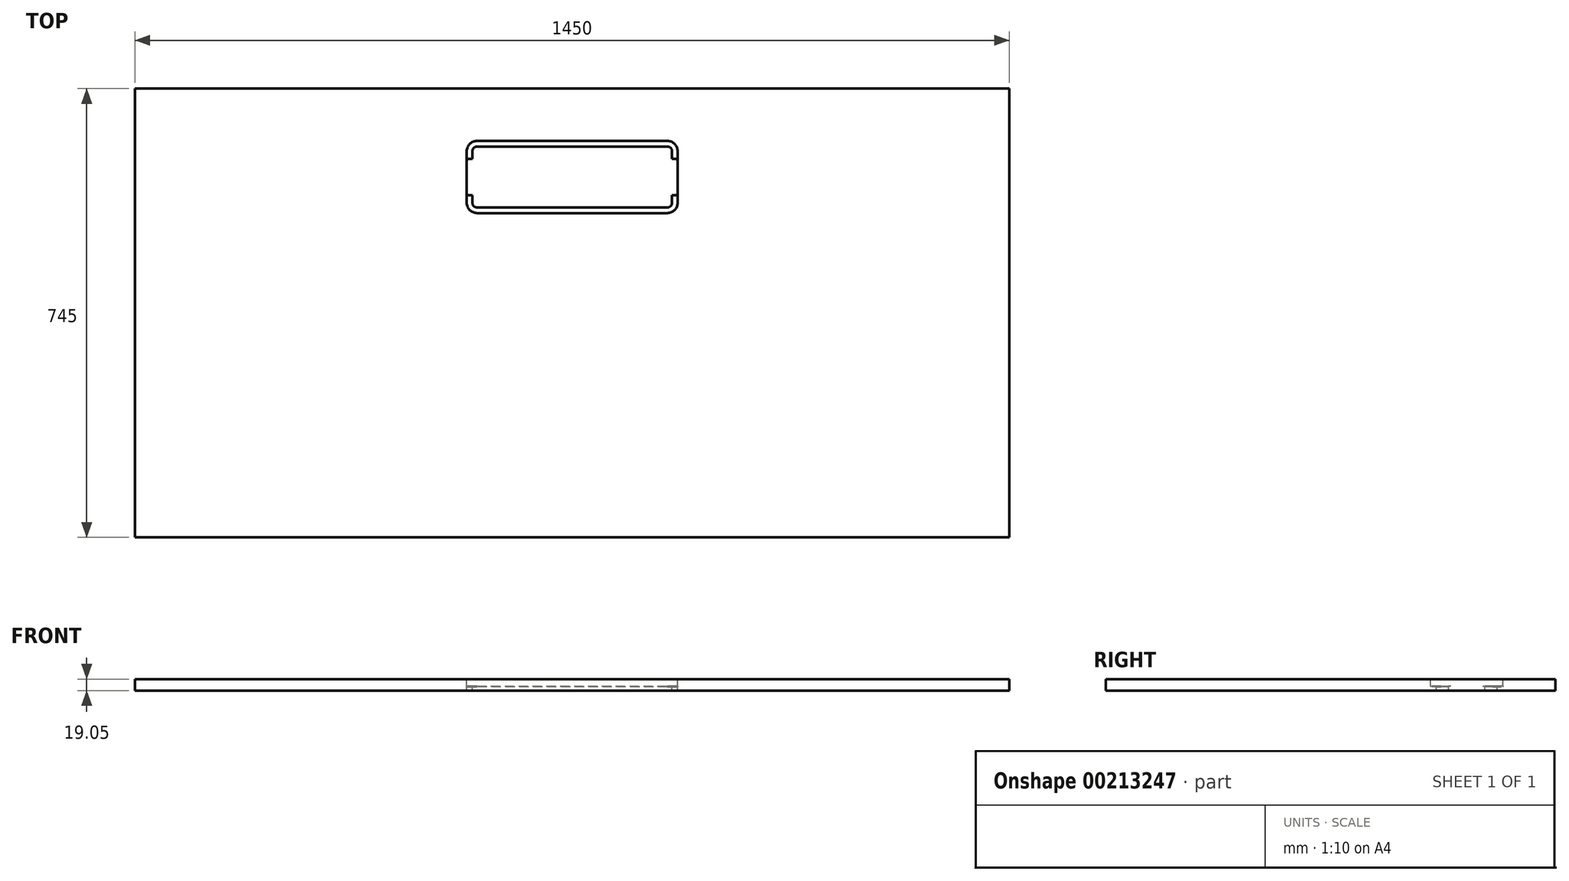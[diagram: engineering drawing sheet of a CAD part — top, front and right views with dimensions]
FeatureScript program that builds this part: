
annotation { "Feature Type Name" : "Feature", "Feature Type Description" : "" }
export const myFeature = defineFeature(function(context is Context, id is Id, definition is map)
    precondition{}
    {
        {
            var Q0;
            Q0=qCreatedBy(makeId("Top.planeOp"),FACE);
            var sketch = newSketch(context, id + "F0", { "sketchPlane" : qUnion([Q0])});
            skLineSegment(sketch, "E0.bottom", {"start": v(-157.8, -59.8) * mm, "end": v(157.8, -59.8) * mm});
            skLineSegment(sketch, "E0.top", {"start": v(-157.8, 59.8) * mm, "end": v(157.8, 59.8) * mm});
            skLineSegment(sketch, "E0.left", {"start": v(-174.8, -42.8) * mm, "end": v(-174.8, 42.8) * mm});
            skLineSegment(sketch, "E0.right", {"start": v(174.8, -42.8) * mm, "end": v(174.8, 42.8) * mm});
            skPoint(sketch, "E0.middle", {"position": v(0, 0) * mm});
            skPoint(sketch, "E1.visualSharp", {"position": v(-174.8, 59.8) * mm});
            skArc(sketch, "E1.filletArc", {"start": v(-157.8, 59.8) * mm, "mid": v(-169.82, 54.82) * mm, "end": v(-174.8, 42.8) * mm});
            skPoint(sketch, "E2.visualSharp", {"position": v(-174.8, -59.8) * mm});
            skArc(sketch, "E2.filletArc", {"start": v(-174.8, -42.8) * mm, "mid": v(-169.82, -54.82) * mm, "end": v(-157.8, -59.8) * mm});
            skPoint(sketch, "E3.visualSharp", {"position": v(174.8, -59.8) * mm});
            skArc(sketch, "E3.filletArc", {"start": v(157.8, -59.8) * mm, "mid": v(169.82, -54.82) * mm, "end": v(174.8, -42.8) * mm});
            skPoint(sketch, "E4.visualSharp", {"position": v(174.8, 59.8) * mm});
            skArc(sketch, "E4.filletArc", {"start": v(174.8, 42.8) * mm, "mid": v(169.82, 54.82) * mm, "end": v(157.8, 59.8) * mm});
            skSolve(sketch);
        }
        {
            var Q0;
            Q0 = qSketchRegion(id + "F0", true);
            extrude(context, id + "F1", {"entities" : qUnion([Q0]), "depth" : 19.05 * mm});
        }
        {
            var Q0;
            Q0=makeQuery(id+"F1.opExtrude","CAP_FACE",FACE,{"disambiguationData":[OSD([sQuery(id+"F0.wireOp",EDGE,"E0.bottom"),sQuery(id+"F0.wireOp",EDGE,"E0.top"),sQuery(id+"F0.wireOp",EDGE,"E0.left"),sQuery(id+"F0.wireOp",EDGE,"E0.right"),sQuery(id+"F0.wireOp",EDGE,"E1.filletArc"),sQuery(id+"F0.wireOp",EDGE,"E2.filletArc"),sQuery(id+"F0.wireOp",EDGE,"E3.filletArc"),sQuery(id+"F0.wireOp",EDGE,"E4.filletArc")])],"isStart":false});
            var sketch = newSketch(context, id + "F2", { "sketchPlane" : qUnion([Q0])});
            skLineSegment(sketch, "E5.bottom", {"start": v(-174.8, -30) * mm, "end": v(-163.3, -30) * mm});
            skLineSegment(sketch, "E5.top", {"start": v(-174.8, 30) * mm, "end": v(-163.3, 30) * mm});
            skLineSegment(sketch, "E5.left", {"start": v(-174.8, -30) * mm, "end": v(-174.8, 30) * mm});
            skLineSegment(sketch, "E5.right", {"start": v(-154.8, -21.5) * mm, "end": v(-154.8, 21.5) * mm});
            skPoint(sketch, "E5.middle", {"position": v(-164.8, 0) * mm});
            skPoint(sketch, "E5.middle.positionSnap0", {"position": v(-174.8, 0) * mm});
            skPoint(sketch, "E5.centerSnap0", {"position": v(-174.8, 0) * mm});
            skPoint(sketch, "E6.visualSharp", {"position": v(-154.8, 30) * mm});
            skArc(sketch, "E6.filletArc", {"start": v(-154.8, 21.5) * mm, "mid": v(-157.29, 27.51) * mm, "end": v(-163.3, 30) * mm});
            skPoint(sketch, "E7.visualSharp", {"position": v(-154.8, -30) * mm});
            skArc(sketch, "E7.filletArc", {"start": v(-163.3, -30) * mm, "mid": v(-157.29, -27.51) * mm, "end": v(-154.8, -21.5) * mm});
            skLineSegment(sketch, "E8", {"start": v(0, 0) * mm, "end": v(0, 113.56) * mm, "construction": true});
            skLineSegment(sketch, "E9.MirrorCS", {"start": v(174.8, 30) * mm, "end": v(163.3, 30) * mm});
            skLineSegment(sketch, "E10.MirrorCS", {"start": v(174.8, -30) * mm, "end": v(174.8, 30) * mm});
            skLineSegment(sketch, "E11.MirrorCS", {"start": v(174.8, -30) * mm, "end": v(163.3, -30) * mm});
            skArc(sketch, "E12.MirrorCS", {"start": v(163.3, -30) * mm, "mid": v(157.29, -27.51) * mm, "end": v(154.8, -21.5) * mm});
            skLineSegment(sketch, "E13.MirrorCS", {"start": v(154.8, -21.5) * mm, "end": v(154.8, 21.5) * mm});
            skArc(sketch, "E14.MirrorCS", {"start": v(154.8, 21.5) * mm, "mid": v(157.29, 27.51) * mm, "end": v(163.3, 30) * mm});
            skSolve(sketch);
        }
        {
            var Q0;
            Q0 = qSketchRegion(id + "F2", true);
            extrude(context, id + "F3", {"entities" : qUnion([Q0]), "operationType" : NewBodyOperationType.REMOVE, "endBound" : BoundingType.THROUGH_ALL, "oppositeDirection" : true, "depth" : 25.4 * mm});
        }
        {
            var Q0;
            Q0=makeQuery(id+"F1.opExtrude","CAP_FACE",FACE,{"disambiguationData":[OSD([sQuery(id+"F0.wireOp",EDGE,"E0.bottom"),sQuery(id+"F0.wireOp",EDGE,"E0.top"),sQuery(id+"F0.wireOp",EDGE,"E0.left"),sQuery(id+"F0.wireOp",EDGE,"E0.right"),sQuery(id+"F0.wireOp",EDGE,"E1.filletArc"),sQuery(id+"F0.wireOp",EDGE,"E2.filletArc"),sQuery(id+"F0.wireOp",EDGE,"E3.filletArc"),sQuery(id+"F0.wireOp",EDGE,"E4.filletArc")])],"isStart":true});
            var sketch = newSketch(context, id + "F4", { "sketchPlane" : qUnion([Q0])});
            skArc(sketch, "E15.0", {"start": v(163.3, 43.3) * mm, "mid": v(147.89, 36.91) * mm, "end": v(141.5, 21.5) * mm, "construction": true});
            skLineSegment(sketch, "E15.1", {"start": v(141.5, -21.5) * mm, "end": v(141.5, 21.5) * mm, "construction": true});
            skArc(sketch, "E15.2", {"start": v(141.5, -21.5) * mm, "mid": v(147.89, -36.91) * mm, "end": v(163.3, -43.3) * mm, "construction": true});
            skLineSegment(sketch, "E15.3", {"start": v(163.3, -43.3) * mm, "end": v(161.5, -43.3) * mm});
            skLineSegment(sketch, "E15.4", {"start": v(161.5, -43.3) * mm, "end": v(161.5, -42.8) * mm});
            skLineSegment(sketch, "E15.5", {"start": v(161.5, 43.3) * mm, "end": v(163.3, 43.3) * mm});
            skArc(sketch, "E15.6", {"start": v(157.8, -46.5) * mm, "mid": v(160.42, -45.42) * mm, "end": v(161.5, -42.8) * mm});
            skLineSegment(sketch, "E15.7", {"start": v(-157.8, -46.5) * mm, "end": v(157.8, -46.5) * mm});
            skArc(sketch, "E15.8", {"start": v(-161.5, -42.8) * mm, "mid": v(-160.42, -45.42) * mm, "end": v(-157.8, -46.5) * mm});
            skLineSegment(sketch, "E15.9", {"start": v(-161.5, -42.8) * mm, "end": v(-161.5, -43.3) * mm, "construction": true});
            skArc(sketch, "E15.10", {"start": v(-157.8, 46.5) * mm, "mid": v(-160.42, 45.42) * mm, "end": v(-161.5, 42.8) * mm});
            skLineSegment(sketch, "E15.11", {"start": v(157.8, 46.5) * mm, "end": v(-157.8, 46.5) * mm});
            skArc(sketch, "E15.12", {"start": v(161.5, 42.8) * mm, "mid": v(160.42, 45.42) * mm, "end": v(157.8, 46.5) * mm});
            skLineSegment(sketch, "E15.13", {"start": v(161.5, 42.8) * mm, "end": v(161.5, 43.3) * mm});
            skLineSegment(sketch, "E15.14", {"start": v(-161.5, 43.3) * mm, "end": v(-161.5, 42.8) * mm, "construction": true});
            skLineSegment(sketch, "E15.15", {"start": v(-163.3, 43.3) * mm, "end": v(-161.5, 43.3) * mm, "construction": true});
            skArc(sketch, "E15.16", {"start": v(-163.3, 43.3) * mm, "mid": v(-147.89, 36.91) * mm, "end": v(-141.5, 21.5) * mm, "construction": true});
            skLineSegment(sketch, "E15.17", {"start": v(-141.5, 21.5) * mm, "end": v(-141.5, -21.5) * mm, "construction": true});
            skArc(sketch, "E15.18", {"start": v(-141.5, -21.5) * mm, "mid": v(-147.89, -36.91) * mm, "end": v(-163.3, -43.3) * mm, "construction": true});
            skLineSegment(sketch, "E15.19", {"start": v(-161.5, -43.3) * mm, "end": v(-163.3, -43.3) * mm, "construction": true});
            skLineSegment(sketch, "E16", {"start": v(-161.5, 42.8) * mm, "end": v(-161.5, -42.8) * mm});
            skLineSegment(sketch, "E17", {"start": v(161.5, -42.8) * mm, "end": v(161.5, 42.8) * mm});
            skLineSegment(sketch, "E18.bottom", {"start": v(-203.2, 88.9) * mm, "end": v(203.2, 88.9) * mm});
            skLineSegment(sketch, "E18.top", {"start": v(-203.2, -88.9) * mm, "end": v(203.2, -88.9) * mm});
            skLineSegment(sketch, "E18.left", {"start": v(-203.2, 88.9) * mm, "end": v(-203.2, -88.9) * mm});
            skLineSegment(sketch, "E18.right", {"start": v(203.2, 88.9) * mm, "end": v(203.2, -88.9) * mm});
            skPoint(sketch, "E18.middle", {"position": v(0, 0) * mm});
            skSolve(sketch);
        }
        {
            var Q0;
            Q0 = qSketchRegion(id + "F4", true);
            extrude(context, id + "F5", {"entities" : qUnion([Q0]), "operationType" : NewBodyOperationType.REMOVE, "oppositeDirection" : true, "depth" : 6 * mm});
        }
        {
            var Q0;
            Q0=makeQuery(id+"F1.opExtrude","CAP_FACE",FACE,{"disambiguationData":[OSD([sQuery(id+"F0.wireOp",EDGE,"E0.bottom"),sQuery(id+"F0.wireOp",EDGE,"E0.top"),sQuery(id+"F0.wireOp",EDGE,"E0.left"),sQuery(id+"F0.wireOp",EDGE,"E0.right"),sQuery(id+"F0.wireOp",EDGE,"E1.filletArc"),sQuery(id+"F0.wireOp",EDGE,"E2.filletArc"),sQuery(id+"F0.wireOp",EDGE,"E3.filletArc"),sQuery(id+"F0.wireOp",EDGE,"E4.filletArc")])],"isStart":false});
            var sketch = newSketch(context, id + "F6", { "sketchPlane" : qUnion([Q0])});
            skLineSegment(sketch, "E19.bottom", {"start": v(725, -598.2) * mm, "end": v(-725, -598.2) * mm});
            skLineSegment(sketch, "E19.top", {"start": v(725, 146.8) * mm, "end": v(-725, 146.8) * mm});
            skLineSegment(sketch, "E19.left", {"start": v(725, -598.2) * mm, "end": v(725, 146.8) * mm});
            skLineSegment(sketch, "E19.right", {"start": v(-725, -598.2) * mm, "end": v(-725, 146.8) * mm});
            skSolve(sketch);
        }
        {
            var Q0;
            Q0 = qSketchRegion(id + "F6", true);
            extrude(context, id + "F7", {"entities" : qUnion([Q0]), "oppositeDirection" : true, "depth" : 19.05 * mm});
        }
        {
            var Q0;
            Q0=makeQuery(id+"F7.opExtrude","CAP_FACE",FACE,{"disambiguationData":[OSD([sQuery(id+"F6.wireOp",EDGE,"E19.bottom"),sQuery(id+"F6.wireOp",EDGE,"E19.top"),sQuery(id+"F6.wireOp",EDGE,"E19.left"),sQuery(id+"F6.wireOp",EDGE,"E19.right")])],"isStart":true});
            var sketch = newSketch(context, id + "F8", { "sketchPlane" : qUnion([Q0])});
            skLineSegment(sketch, "E20.0", {"start": v(-157.8, 59.8) * mm, "end": v(157.8, 59.8) * mm});
            skLineSegment(sketch, "E21.0", {"start": v(-157.8, -59.8) * mm, "end": v(157.8, -59.8) * mm});
            skArc(sketch, "E22.0", {"start": v(-174.8, -42.8) * mm, "mid": v(-169.82, -54.82) * mm, "end": v(-157.8, -59.8) * mm});
            skArc(sketch, "E23.0", {"start": v(-157.8, 59.8) * mm, "mid": v(-169.82, 54.82) * mm, "end": v(-174.8, 42.8) * mm});
            skLineSegment(sketch, "E24.0", {"start": v(-174.8, 30) * mm, "end": v(-174.8, 42.8) * mm});
            skLineSegment(sketch, "E25.0", {"start": v(-174.8, -42.8) * mm, "end": v(-174.8, -30) * mm});
            skArc(sketch, "E26.0", {"start": v(157.8, -59.8) * mm, "mid": v(169.82, -54.82) * mm, "end": v(174.8, -42.8) * mm});
            skLineSegment(sketch, "E27.0", {"start": v(174.8, -42.8) * mm, "end": v(174.8, -30) * mm});
            skLineSegment(sketch, "E28.0", {"start": v(174.8, 30) * mm, "end": v(174.8, 42.8) * mm});
            skArc(sketch, "E29.0", {"start": v(174.8, 42.8) * mm, "mid": v(169.82, 54.82) * mm, "end": v(157.8, 59.8) * mm});
            skLineSegment(sketch, "E30", {"start": v(-174.8, 30) * mm, "end": v(-174.8, -30) * mm});
            skLineSegment(sketch, "E31", {"start": v(174.8, 30) * mm, "end": v(174.8, -30) * mm});
            skSolve(sketch);
        }
        {
            var Q0;
            Q0 = qSketchRegion(id + "F8", true);
            extrude(context, id + "F9", {"entities" : qUnion([Q0]), "operationType" : NewBodyOperationType.REMOVE, "oppositeDirection" : true, "depth" : 12 * mm});
        }
        {
            var Q0;
            Q0=makeQuery(id+"F9.boolean.opBoolean","COPY",FACE,{"derivedFrom":makeQuery(id+"F9.opExtrude","CAP_FACE",FACE,{"disambiguationData":[OSD([sQuery(id+"F8.wireOp",EDGE,"E20.0"),sQuery(id+"F8.wireOp",EDGE,"E21.0"),sQuery(id+"F8.wireOp",EDGE,"E22.0"),sQuery(id+"F8.wireOp",EDGE,"E23.0"),sQuery(id+"F8.wireOp",EDGE,"E24.0"),sQuery(id+"F8.wireOp",EDGE,"E25.0"),sQuery(id+"F8.wireOp",EDGE,"E26.0"),sQuery(id+"F8.wireOp",EDGE,"E27.0"),sQuery(id+"F8.wireOp",EDGE,"E28.0"),sQuery(id+"F8.wireOp",EDGE,"E29.0"),sQuery(id+"F8.wireOp",EDGE,"E30"),sQuery(id+"F8.wireOp",EDGE,"E31")])],"isStart":false})});
            var sketch = newSketch(context, id + "F10", { "sketchPlane" : qUnion([Q0])});
            skLineSegment(sketch, "E32.0", {"start": v(-165.5, -42.8) * mm, "end": v(-165.5, -30) * mm});
            skLineSegment(sketch, "E32.1", {"start": v(165.5, -30) * mm, "end": v(165.5, -42.8) * mm});
            skArc(sketch, "E32.2", {"start": v(165.5, -42.8) * mm, "mid": v(163.24, -48.24) * mm, "end": v(157.8, -50.5) * mm});
            skLineSegment(sketch, "E32.3", {"start": v(157.8, -50.5) * mm, "end": v(-157.8, -50.5) * mm});
            skArc(sketch, "E32.4", {"start": v(-157.8, -50.5) * mm, "mid": v(-163.24, -48.24) * mm, "end": v(-165.5, -42.8) * mm});
            skLineSegment(sketch, "E33.0", {"start": v(165.5, 42.8) * mm, "end": v(165.5, 30) * mm});
            skLineSegment(sketch, "E33.1", {"start": v(-165.5, 30) * mm, "end": v(-165.5, 42.8) * mm});
            skArc(sketch, "E33.2", {"start": v(-165.5, 42.8) * mm, "mid": v(-163.24, 48.24) * mm, "end": v(-157.8, 50.5) * mm});
            skLineSegment(sketch, "E33.3", {"start": v(-157.8, 50.5) * mm, "end": v(157.8, 50.5) * mm});
            skArc(sketch, "E33.4", {"start": v(157.8, 50.5) * mm, "mid": v(163.24, 48.24) * mm, "end": v(165.5, 42.8) * mm});
            skLineSegment(sketch, "E34", {"start": v(-165.5, -30) * mm, "end": v(-165.5, 30) * mm});
            skLineSegment(sketch, "E35", {"start": v(165.5, 30) * mm, "end": v(165.5, -30) * mm});
            skSolve(sketch);
        }
        {
            var Q0;
            Q0 = qSketchRegion(id + "F10", true);
            extrude(context, id + "F11", {"entities" : qUnion([Q0]), "operationType" : NewBodyOperationType.REMOVE, "endBound" : BoundingType.THROUGH_ALL, "oppositeDirection" : true, "depth" : 25.4 * mm});
        }
        {
            var Q0;
            Q0=makeQuery(id+"F9.boolean.opBoolean","COPY",FACE,{"derivedFrom":makeQuery(id+"F9.opExtrude","CAP_FACE",FACE,{"disambiguationData":[OSD([sQuery(id+"F8.wireOp",EDGE,"E20.0"),sQuery(id+"F8.wireOp",EDGE,"E21.0"),sQuery(id+"F8.wireOp",EDGE,"E22.0"),sQuery(id+"F8.wireOp",EDGE,"E23.0"),sQuery(id+"F8.wireOp",EDGE,"E24.0"),sQuery(id+"F8.wireOp",EDGE,"E25.0"),sQuery(id+"F8.wireOp",EDGE,"E26.0"),sQuery(id+"F8.wireOp",EDGE,"E27.0"),sQuery(id+"F8.wireOp",EDGE,"E28.0"),sQuery(id+"F8.wireOp",EDGE,"E29.0"),sQuery(id+"F8.wireOp",EDGE,"E30"),sQuery(id+"F8.wireOp",EDGE,"E31")])],"isStart":false})});
            var sketch = newSketch(context, id + "F12", { "sketchPlane" : qUnion([Q0])});
            skLineSegment(sketch, "E36.0", {"start": v(-174.8, 30) * mm, "end": v(-165.5, 30) * mm});
            skLineSegment(sketch, "E37.0", {"start": v(-174.8, -30) * mm, "end": v(-165.5, -30) * mm});
            skLineSegment(sketch, "E38.0", {"start": v(-174.8, -30) * mm, "end": v(-174.8, 30) * mm});
            skPoint(sketch, "E39.orphan", {"position": v(-174.8, 42.8) * mm});
            skPoint(sketch, "E40.orphan", {"position": v(-174.8, -42.8) * mm});
            skLineSegment(sketch, "E41.0", {"start": v(-165.5, -30) * mm, "end": v(-165.5, 30) * mm});
            skPoint(sketch, "E42.orphan", {"position": v(-165.5, 42.8) * mm});
            skPoint(sketch, "E43.orphan", {"position": v(-163.3, 30) * mm});
            skPoint(sketch, "E44.orphan", {"position": v(-165.5, -42.8) * mm});
            skPoint(sketch, "E45.orphan", {"position": v(-163.3, -30) * mm});
            skLineSegment(sketch, "E46", {"start": v(0, 0) * mm, "end": v(0, 330.61) * mm, "construction": true});
            skLineSegment(sketch, "E47.MirrorCS", {"start": v(165.5, -30) * mm, "end": v(165.5, 30) * mm});
            skLineSegment(sketch, "E48.MirrorCS", {"start": v(174.8, 30) * mm, "end": v(165.5, 30) * mm});
            skLineSegment(sketch, "E49.MirrorCS", {"start": v(174.8, -30) * mm, "end": v(174.8, 30) * mm});
            skLineSegment(sketch, "E50.MirrorCS", {"start": v(174.8, -30) * mm, "end": v(165.5, -30) * mm});
            skSolve(sketch);
        }
        {
            var Q0;
            Q0 = qSketchRegion(id + "F12", true);
            extrude(context, id + "F13", {"entities" : qUnion([Q0]), "operationType" : NewBodyOperationType.REMOVE, "endBound" : BoundingType.THROUGH_ALL, "oppositeDirection" : true, "depth" : 25.4 * mm});
        }
        {
            var Q0;
            Q0=makeQuery(id+"F13.boolean.opBoolean","COPY",EDGE,{"derivedFrom":makeQuery(id+"F13.opExtrude","SWEPT_EDGE",EDGE,{"disambiguationData":[OSD([sQuery(id+"F10.wireOp",EDGE,"E32.0"),sQuery(id+"F10.wireOp",EDGE,"E33.1"),sQuery(id+"F10.wireOp",EDGE,"E34"),sQuery(id+"F12.wireOp",EDGE,"E36.0"),sQuery(id+"F12.wireOp",EDGE,"E41.0")])]})});
            var Q1;
            Q1=makeQuery(id+"F13.boolean.opBoolean","COPY",EDGE,{"derivedFrom":makeQuery(id+"F13.opExtrude","SWEPT_EDGE",EDGE,{"disambiguationData":[OSD([sQuery(id+"F8.wireOp",EDGE,"E24.0"),sQuery(id+"F8.wireOp",EDGE,"E25.0"),sQuery(id+"F8.wireOp",EDGE,"E30"),sQuery(id+"F12.wireOp",EDGE,"E36.0"),sQuery(id+"F12.wireOp",EDGE,"E38.0")])]})});
            var Q2;
            Q2=makeQuery(id+"F13.boolean.opBoolean","COPY",EDGE,{"derivedFrom":makeQuery(id+"F13.opExtrude","SWEPT_EDGE",EDGE,{"disambiguationData":[OSD([sQuery(id+"F8.wireOp",EDGE,"E24.0"),sQuery(id+"F8.wireOp",EDGE,"E25.0"),sQuery(id+"F8.wireOp",EDGE,"E30"),sQuery(id+"F12.wireOp",EDGE,"E37.0"),sQuery(id+"F12.wireOp",EDGE,"E38.0")])]})});
            var Q3;
            Q3=makeQuery(id+"F13.boolean.opBoolean","COPY",EDGE,{"derivedFrom":makeQuery(id+"F13.opExtrude","SWEPT_EDGE",EDGE,{"disambiguationData":[OSD([sQuery(id+"F10.wireOp",EDGE,"E32.0"),sQuery(id+"F10.wireOp",EDGE,"E33.1"),sQuery(id+"F10.wireOp",EDGE,"E34"),sQuery(id+"F12.wireOp",EDGE,"E37.0"),sQuery(id+"F12.wireOp",EDGE,"E41.0")])]})});
            var Q4;
            Q4=makeQuery(id+"F13.boolean.opBoolean","COPY",EDGE,{"derivedFrom":makeQuery(id+"F13.opExtrude","SWEPT_EDGE",EDGE,{"disambiguationData":[OSD([sQuery(id+"F10.wireOp",EDGE,"E32.1"),sQuery(id+"F10.wireOp",EDGE,"E33.0"),sQuery(id+"F10.wireOp",EDGE,"E35"),sQuery(id+"F12.wireOp",EDGE,"E47.MirrorCS"),sQuery(id+"F12.wireOp",EDGE,"E48.MirrorCS")])]})});
            var Q5;
            Q5=makeQuery(id+"F13.boolean.opBoolean","COPY",EDGE,{"derivedFrom":makeQuery(id+"F13.opExtrude","SWEPT_EDGE",EDGE,{"disambiguationData":[OSD([sQuery(id+"F8.wireOp",EDGE,"E27.0"),sQuery(id+"F8.wireOp",EDGE,"E28.0"),sQuery(id+"F8.wireOp",EDGE,"E31"),sQuery(id+"F12.wireOp",EDGE,"E48.MirrorCS"),sQuery(id+"F12.wireOp",EDGE,"E49.MirrorCS")])]})});
            var Q6;
            Q6=makeQuery(id+"F13.boolean.opBoolean","COPY",EDGE,{"derivedFrom":makeQuery(id+"F13.opExtrude","SWEPT_EDGE",EDGE,{"disambiguationData":[OSD([sQuery(id+"F10.wireOp",EDGE,"E32.1"),sQuery(id+"F10.wireOp",EDGE,"E33.0"),sQuery(id+"F10.wireOp",EDGE,"E35"),sQuery(id+"F12.wireOp",EDGE,"E47.MirrorCS"),sQuery(id+"F12.wireOp",EDGE,"E50.MirrorCS")])]})});
            var Q7;
            Q7=makeQuery(id+"F13.boolean.opBoolean","COPY",EDGE,{"derivedFrom":makeQuery(id+"F13.opExtrude","SWEPT_EDGE",EDGE,{"disambiguationData":[OSD([sQuery(id+"F8.wireOp",EDGE,"E27.0"),sQuery(id+"F8.wireOp",EDGE,"E28.0"),sQuery(id+"F8.wireOp",EDGE,"E31"),sQuery(id+"F12.wireOp",EDGE,"E49.MirrorCS"),sQuery(id+"F12.wireOp",EDGE,"E50.MirrorCS")])]})});
            fillet(context, id + "F14", {"entities" : qUnion([Q0, Q1, Q2, Q3, Q4, Q5, Q6, Q7]), "radius" : 3.5 * mm, "tangentPropagation" : true, "allowEdgeOverflow" : false});
        }
    });
